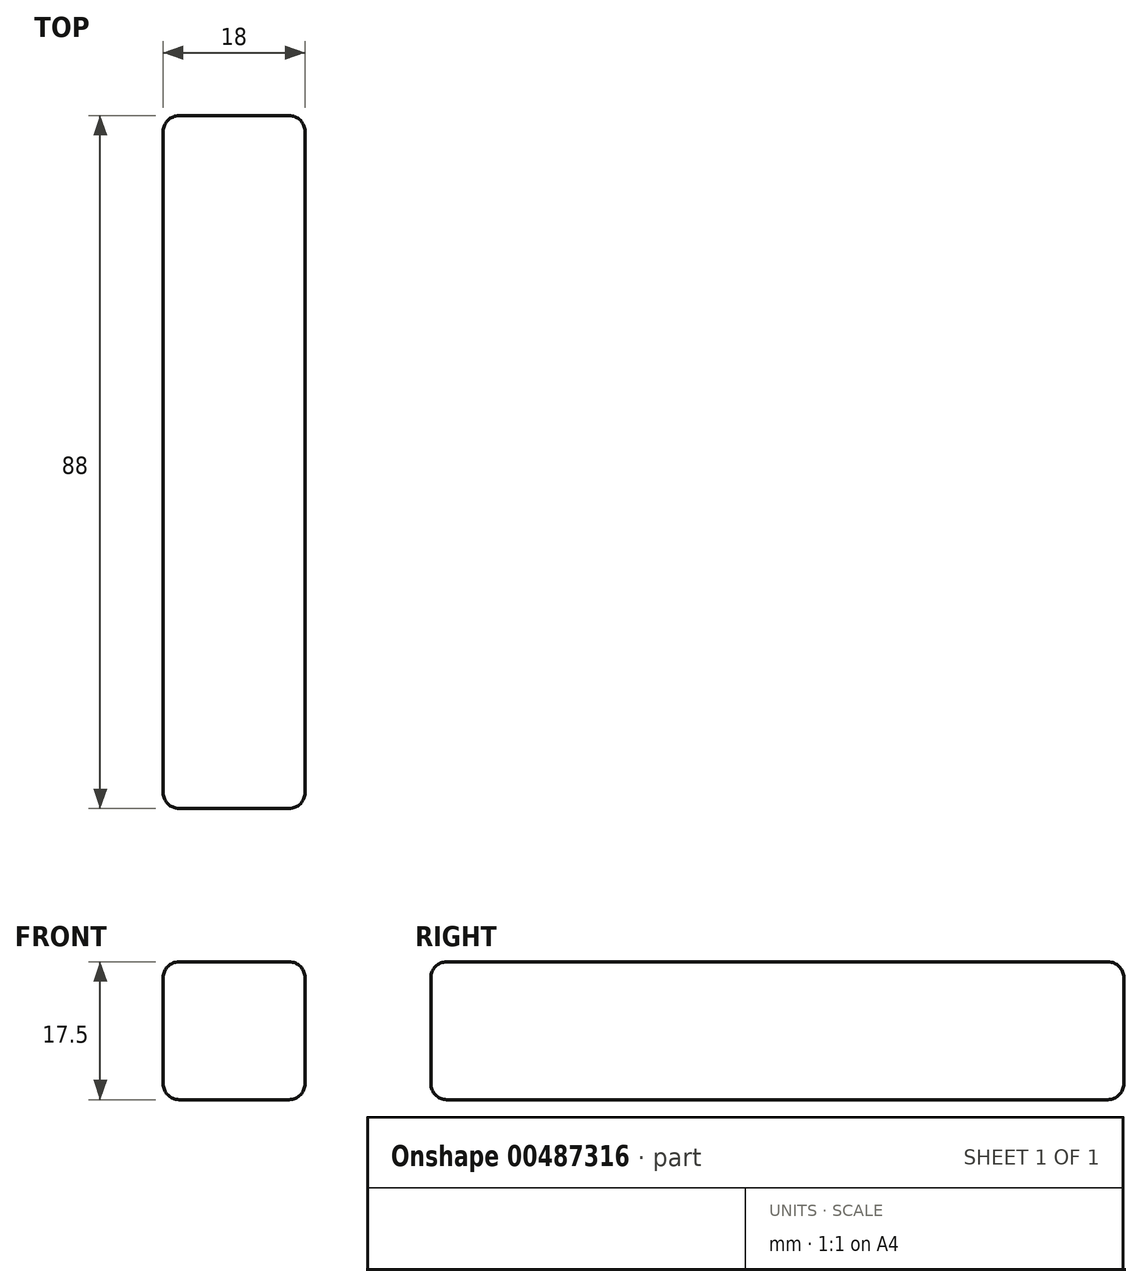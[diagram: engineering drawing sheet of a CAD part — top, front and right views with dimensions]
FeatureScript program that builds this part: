
annotation { "Feature Type Name" : "Feature", "Feature Type Description" : "" }
export const myFeature = defineFeature(function(context is Context, id is Id, definition is map)
    precondition{}
    {
        {
            var Q0;
            Q0=qCreatedBy(makeId("Top.planeOp"),FACE);
            var sketch = newSketch(context, id + "F0", { "sketchPlane" : qUnion([Q0])});
            skLineSegment(sketch, "E0.bottom", {"start": v(-9, 44.15) * mm, "end": v(9, 44.15) * mm});
            skLineSegment(sketch, "E0.top", {"start": v(-9, -43.85) * mm, "end": v(9, -43.85) * mm});
            skLineSegment(sketch, "E0.left", {"start": v(-9, 44.15) * mm, "end": v(-9, -43.85) * mm});
            skLineSegment(sketch, "E0.right", {"start": v(9, 44.15) * mm, "end": v(9, -43.85) * mm});
            skPoint(sketch, "E0.middle", {"position": v(0, 0.15) * mm});
            skSolve(sketch);
        }
        {
            var Q0;
            Q0=makeQuery(id+"F0.imprint","IMPRINT",FACE,{"disambiguationData":[TD([[makeQuery(id+"F0.imprint","IMPRINT",EDGE,{"derivedFrom":sQuery(id+"F0.wireOp",EDGE,"E0.bottom")}),-1.0]])]});
            extrude(context, id + "F1", {"entities" : qUnion([Q0]), "endBound" : BoundingType.SYMMETRIC, "depth" : 17.5 * mm});
        }
        {
            var Q0;
            Q0=makeQuery(id+"F1.opExtrude","CAP_EDGE",EDGE,{"disambiguationData":[OSD([sQuery(id+"F0.wireOp",EDGE,"E0.left")])],"isStart":false});
            var Q1;
            Q1=makeQuery(id+"F1.opExtrude","CAP_EDGE",EDGE,{"disambiguationData":[OSD([sQuery(id+"F0.wireOp",EDGE,"E0.left")])],"isStart":true});
            var Q2;
            Q2=makeQuery(id+"F1.opExtrude","CAP_EDGE",EDGE,{"disambiguationData":[OSD([sQuery(id+"F0.wireOp",EDGE,"E0.top")])],"isStart":false});
            var Q3;
            Q3=makeQuery(id+"F1.opExtrude","SWEPT_EDGE",EDGE,{"disambiguationData":[OSD([sQuery(id+"F0.wireOp",EDGE,"E0.top"),sQuery(id+"F0.wireOp",EDGE,"E0.left")])]});
            var Q4;
            Q4=makeQuery(id+"F1.opExtrude","SWEPT_EDGE",EDGE,{"disambiguationData":[OSD([sQuery(id+"F0.wireOp",EDGE,"E0.top"),sQuery(id+"F0.wireOp",EDGE,"E0.right")])]});
            var Q5;
            Q5=makeQuery(id+"F1.opExtrude","CAP_EDGE",EDGE,{"disambiguationData":[OSD([sQuery(id+"F0.wireOp",EDGE,"E0.top")])],"isStart":true});
            var Q6;
            Q6=makeQuery(id+"F1.opExtrude","CAP_EDGE",EDGE,{"disambiguationData":[OSD([sQuery(id+"F0.wireOp",EDGE,"E0.right")])],"isStart":true});
            var Q7;
            Q7=makeQuery(id+"F1.opExtrude","CAP_EDGE",EDGE,{"disambiguationData":[OSD([sQuery(id+"F0.wireOp",EDGE,"E0.right")])],"isStart":false});
            var Q8;
            Q8=makeQuery(id+"F1.opExtrude","SWEPT_EDGE",EDGE,{"disambiguationData":[OSD([sQuery(id+"F0.wireOp",EDGE,"E0.bottom"),sQuery(id+"F0.wireOp",EDGE,"E0.right")])]});
            var Q9;
            Q9=makeQuery(id+"F1.opExtrude","CAP_EDGE",EDGE,{"disambiguationData":[OSD([sQuery(id+"F0.wireOp",EDGE,"E0.bottom")])],"isStart":false});
            var Q10;
            Q10=makeQuery(id+"F1.opExtrude","SWEPT_EDGE",EDGE,{"disambiguationData":[OSD([sQuery(id+"F0.wireOp",EDGE,"E0.bottom"),sQuery(id+"F0.wireOp",EDGE,"E0.left")])]});
            var Q11;
            Q11=makeQuery(id+"F1.opExtrude","CAP_EDGE",EDGE,{"disambiguationData":[OSD([sQuery(id+"F0.wireOp",EDGE,"E0.bottom")])],"isStart":true});
            fillet(context, id + "F2", {"entities" : qUnion([Q0, Q1, Q2, Q3, Q4, Q5, Q6, Q7, Q8, Q9, Q10, Q11]), "radius" : 2 * mm, "tangentPropagation" : true, "allowEdgeOverflow" : false});
        }
    });
